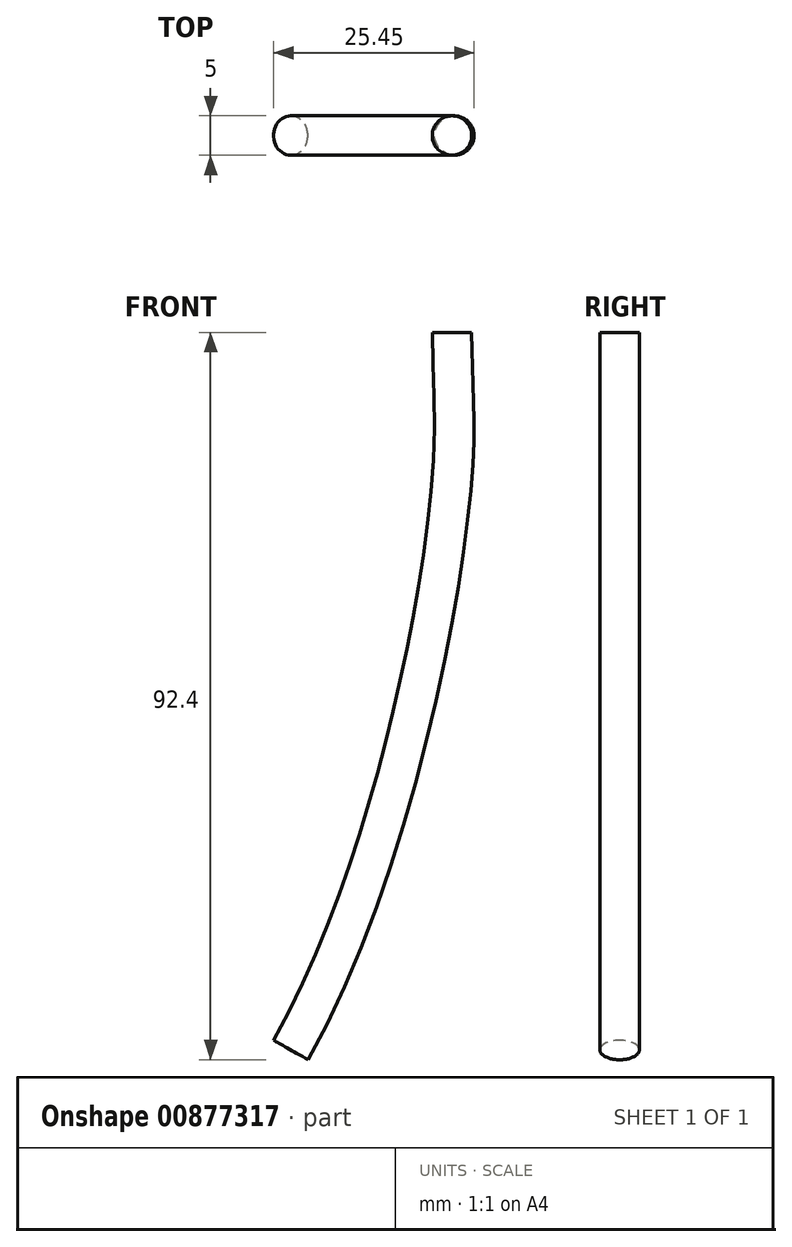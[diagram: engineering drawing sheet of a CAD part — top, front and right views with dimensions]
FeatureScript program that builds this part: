
annotation { "Feature Type Name" : "Feature", "Feature Type Description" : "" }
export const myFeature = defineFeature(function(context is Context, id is Id, definition is map)
    precondition{}
    {
        {
            var Q0;
            Q0=qCreatedBy(makeId("Top.planeOp"),FACE);
            var sketch = newSketch(context, id + "F0", { "sketchPlane" : qUnion([Q0])});
            skCircle(sketch, "E0", {"center": v(0, 0) * mm, "radius": 2.5 * mm});
            skSolve(sketch);
        }
        {
            var Q0;
            Q0=qCreatedBy(makeId("Front.planeOp"),FACE);
            var sketch = newSketch(context, id + "F1", { "sketchPlane" : qUnion([Q0])});
            skFitSpline(sketch, "E1", {"points": [v(0, 0) * mm, v(0, -18.7) * mm, v(-20.48, -91.17) * mm], "startDerivative": vector(0, -55.44) * mm, "endDerivative": vector(-55.44, -97.62) * mm});
            skSolve(sketch);
        }
        {
            var Q0;
            Q0=qSketchRegion(id+"F0",true);
            var Q1;
            Q1=sQuery(id+"F1.wireOp",EDGE,"E1");
            sweep(context, id + "F2", {"profiles" : qUnion([Q0]), "path" : qUnion([Q1])});
        }
    });
